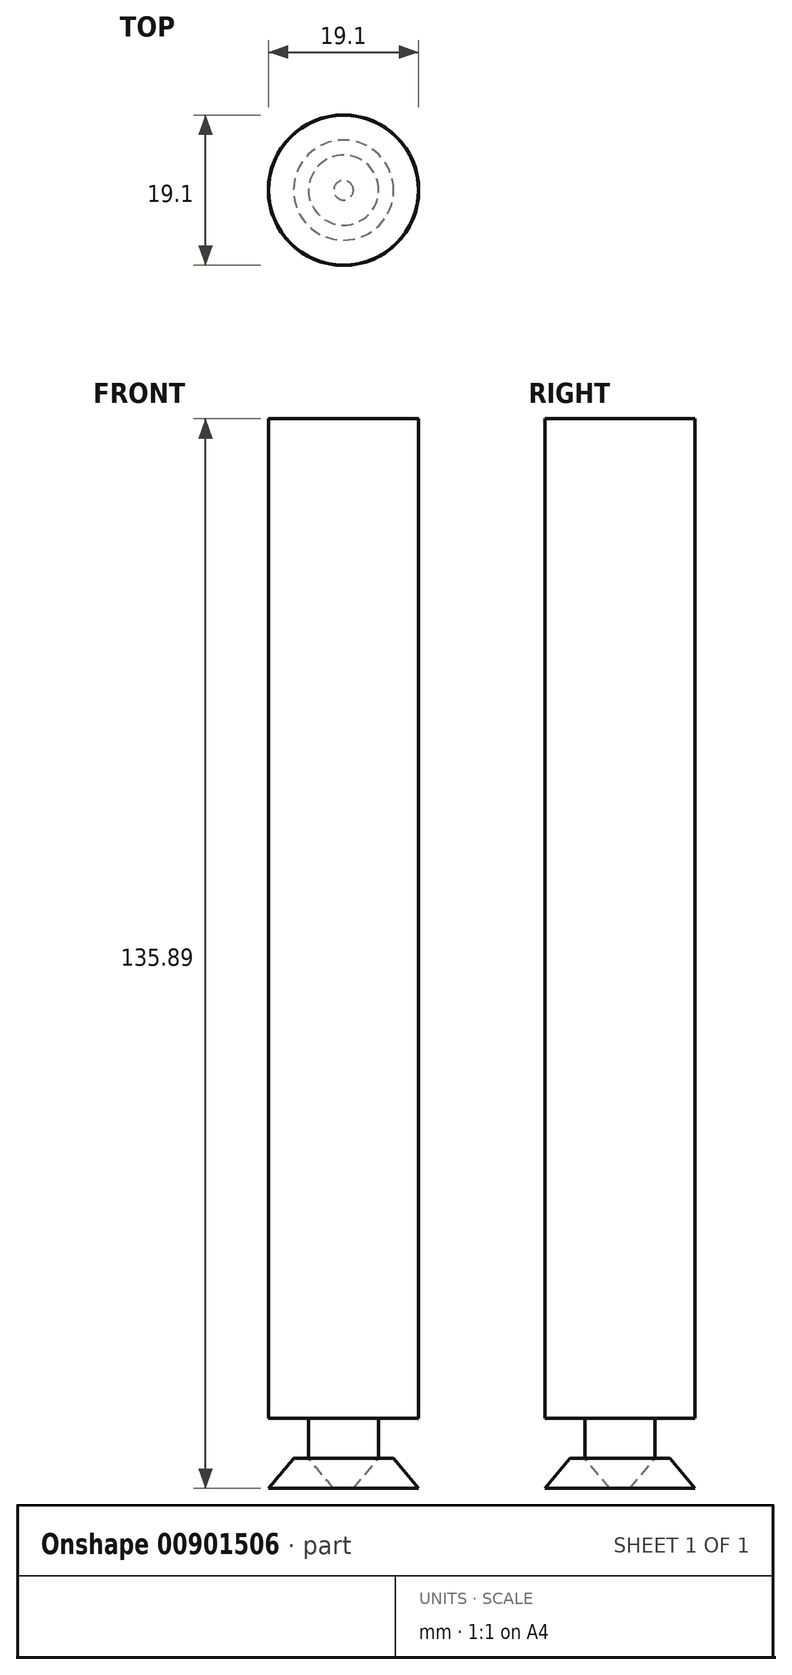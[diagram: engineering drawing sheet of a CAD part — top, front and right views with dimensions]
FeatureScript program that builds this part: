
annotation { "Feature Type Name" : "Feature", "Feature Type Description" : "" }
export const myFeature = defineFeature(function(context is Context, id is Id, definition is map)
    precondition{}
    {
        {
            var Q0;
            Q0=qCreatedBy(makeId("Top.planeOp"),FACE);
            var sketch = newSketch(context, id + "F0", { "sketchPlane" : qUnion([Q0])});
            skCircle(sketch, "E0", {"center": v(0, 0) * mm, "radius": 9.53 * mm});
            skSolve(sketch);
        }
        {
            var Q0;
            Q0=makeQuery(id+"F0.imprint","IMPRINT",FACE,{"disambiguationData":[TD([[makeQuery(id+"F0.imprint","IMPRINT",EDGE,{"derivedFrom":sQuery(id+"F0.wireOp",EDGE,"E0")}),1.0]])]});
            extrude(context, id + "F1", {"entities" : qUnion([Q0]), "oppositeDirection" : true, "depth" : 127 * mm, "offsetDistance" : 25.4 * mm});
        }
        {
            var Q0;
            Q0=makeQuery(id+"F1.opExtrude","CAP_FACE",FACE,{"disambiguationData":[OSD([sQuery(id+"F0.wireOp",EDGE,"E0")])],"isStart":false});
            var sketch = newSketch(context, id + "F2", { "sketchPlane" : qUnion([Q0])});
            skCircle(sketch, "E1", {"center": v(0, 0) * mm, "radius": 4.45 * mm});
            skSolve(sketch);
        }
        {
            var Q0;
            Q0=makeQuery(id+"F2.imprint","IMPRINT",FACE,{"disambiguationData":[TD([[makeQuery(id+"F2.imprint","IMPRINT",EDGE,{"derivedFrom":sQuery(id+"F2.wireOp",EDGE,"E1")}),1.0]])]});
            extrude(context, id + "F3", {"entities" : qUnion([Q0]), "depth" : 5.08 * mm, "offsetDistance" : 25.4 * mm});
        }
        {
            var Q0;
            Q0=makeQuery(id+"F3.opExtrude","CAP_FACE",FACE,{"disambiguationData":[OSD([sQuery(id+"F2.wireOp",EDGE,"E1")])],"isStart":false});
            var sketch = newSketch(context, id + "F4", { "sketchPlane" : qUnion([Q0])});
            skCircle(sketch, "E2", {"center": v(0, 0) * mm, "radius": 6.35 * mm});
            skSolve(sketch);
        }
        {
            var Q0;
            Q0=makeQuery(id+"F4.imprint","IMPRINT",FACE,{"disambiguationData":[TD([[makeQuery(id+"F4.imprint","IMPRINT",EDGE,{"derivedFrom":sQuery(id+"F4.wireOp",EDGE,"E2")}),1.0]])]});
            extrude(context, id + "F5", {"entities" : qUnion([Q0]), "depth" : 3.8 * mm, "offsetDistance" : 25.4 * mm, "hasDraft" : true, "draftAngle" : 40 * degree});
        }
    });
